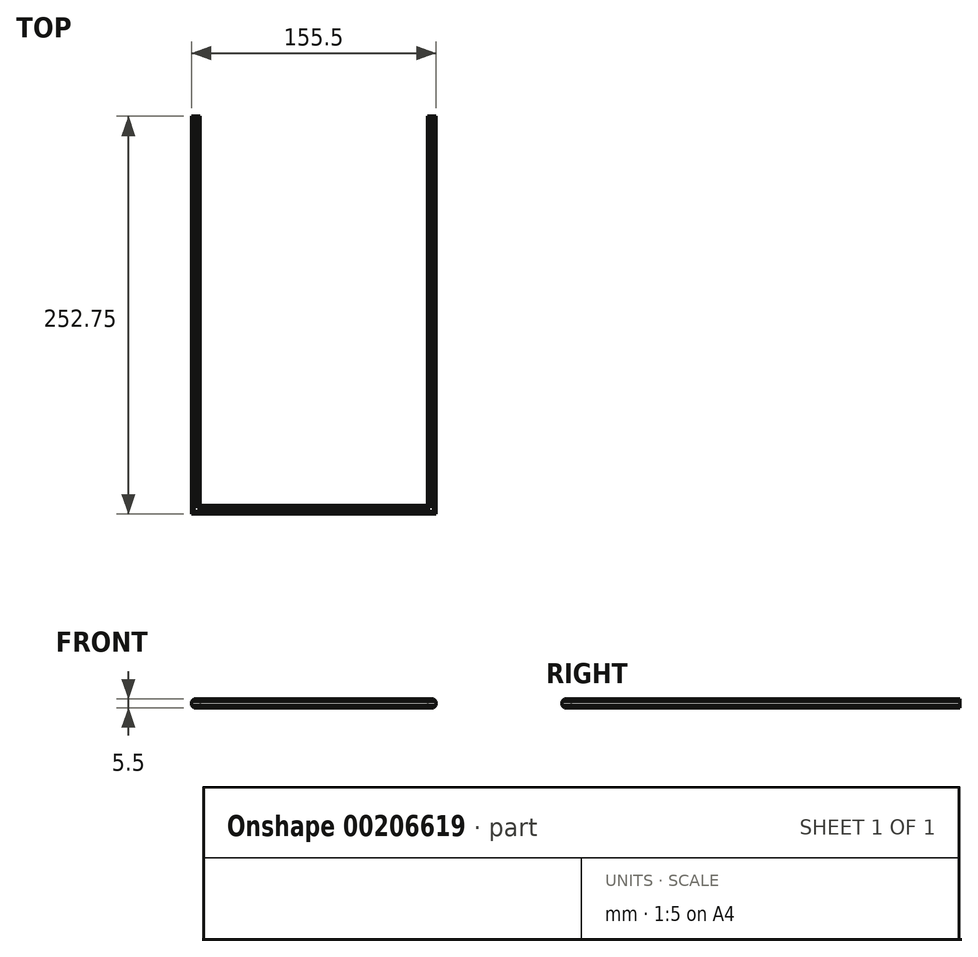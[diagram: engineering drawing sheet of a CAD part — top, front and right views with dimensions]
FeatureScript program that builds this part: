
annotation { "Feature Type Name" : "Feature", "Feature Type Description" : "" }
export const myFeature = defineFeature(function(context is Context, id is Id, definition is map)
    precondition{}
    {
        {
            var Q0;
            Q0=qCreatedBy(makeId("Top.planeOp"),FACE);
            var sketch = newSketch(context, id + "F0", { "sketchPlane" : qUnion([Q0])});
            skLineSegment(sketch, "E0.top", {"start": v(0, -250) * mm, "end": v(150, -250) * mm});
            skLineSegment(sketch, "E0.left", {"start": v(0, 0) * mm, "end": v(0, -250) * mm});
            skLineSegment(sketch, "E0.right", {"start": v(150, 0) * mm, "end": v(150, -250) * mm});
            skPoint(sketch, "E1", {"position": v(150, -125) * mm});
            skPoint(sketch, "E2", {"position": v(0, -125) * mm});
            skPoint(sketch, "E3", {"position": v(150, -30) * mm});
            skPoint(sketch, "E4", {"position": v(150, -90) * mm});
            skPoint(sketch, "E5", {"position": v(150, -60) * mm});
            skPoint(sketch, "E6", {"position": v(150, -155) * mm});
            skPoint(sketch, "E7", {"position": v(150, -237.5) * mm});
            skPoint(sketch, "E8", {"position": v(150, -268.75) * mm});
            skPoint(sketch, "E9", {"position": v(0, -155) * mm});
            skPoint(sketch, "E10", {"position": v(0, -237.5) * mm});
            skPoint(sketch, "E11", {"position": v(0, -268.75) * mm});
            skPoint(sketch, "E12", {"position": v(150, -120) * mm});
            skPoint(sketch, "E13", {"position": v(150, -216.3) * mm});
            skSolve(sketch);
        }
        {
            var Q0;
            Q0=qCreatedBy(makeId("Front.planeOp"),FACE);
            var sketch = newSketch(context, id + "F1", { "sketchPlane" : qUnion([Q0])});
            skCircle(sketch, "E14.cCircle", {"center": v(0, 0) * mm, "radius": 2.75 * mm, "construction": true});
            skLineSegment(sketch, "E14.0", {"start": v(-1.14, 2.75) * mm, "end": v(1.14, 2.75) * mm});
            skLineSegment(sketch, "E14.1", {"start": v(1.14, 2.75) * mm, "end": v(2.75, 1.14) * mm});
            skLineSegment(sketch, "E14.2", {"start": v(2.75, 1.14) * mm, "end": v(2.75, -1.14) * mm});
            skLineSegment(sketch, "E14.3", {"start": v(2.75, -1.14) * mm, "end": v(1.14, -2.75) * mm});
            skLineSegment(sketch, "E14.4", {"start": v(1.14, -2.75) * mm, "end": v(-1.14, -2.75) * mm});
            skLineSegment(sketch, "E14.5", {"start": v(-1.14, -2.75) * mm, "end": v(-2.75, -1.14) * mm});
            skLineSegment(sketch, "E14.6", {"start": v(-2.75, -1.14) * mm, "end": v(-2.75, 1.14) * mm});
            skLineSegment(sketch, "E14.7", {"start": v(-2.75, 1.14) * mm, "end": v(-1.14, 2.75) * mm});
            skPoint(sketch, "E14.0.midPoint", {"position": v(0, 2.75) * mm});
            skSolve(sketch);
        }
        {
            var Q0;
            Q0=makeQuery(id+"F1.imprint","IMPRINT",FACE,{"disambiguationData":[TD([[makeQuery(id+"F1.imprint","IMPRINT",EDGE,{"derivedFrom":sQuery(id+"F1.wireOp",EDGE,"E14.0")}),-1.0]])]});
            var Q1;
            Q1=sQuery(id+"F0.wireOp",EDGE,"E0.left");
            var Q2;
            Q2=sQuery(id+"F0.wireOp",EDGE,"E0.top");
            var Q3;
            Q3=sQuery(id+"F0.wireOp",EDGE,"E0.right");
            sweep(context, id + "F2", {"profiles" : qUnion([Q0]), "path" : qUnion([Q1, Q2, Q3])});
        }
    });
